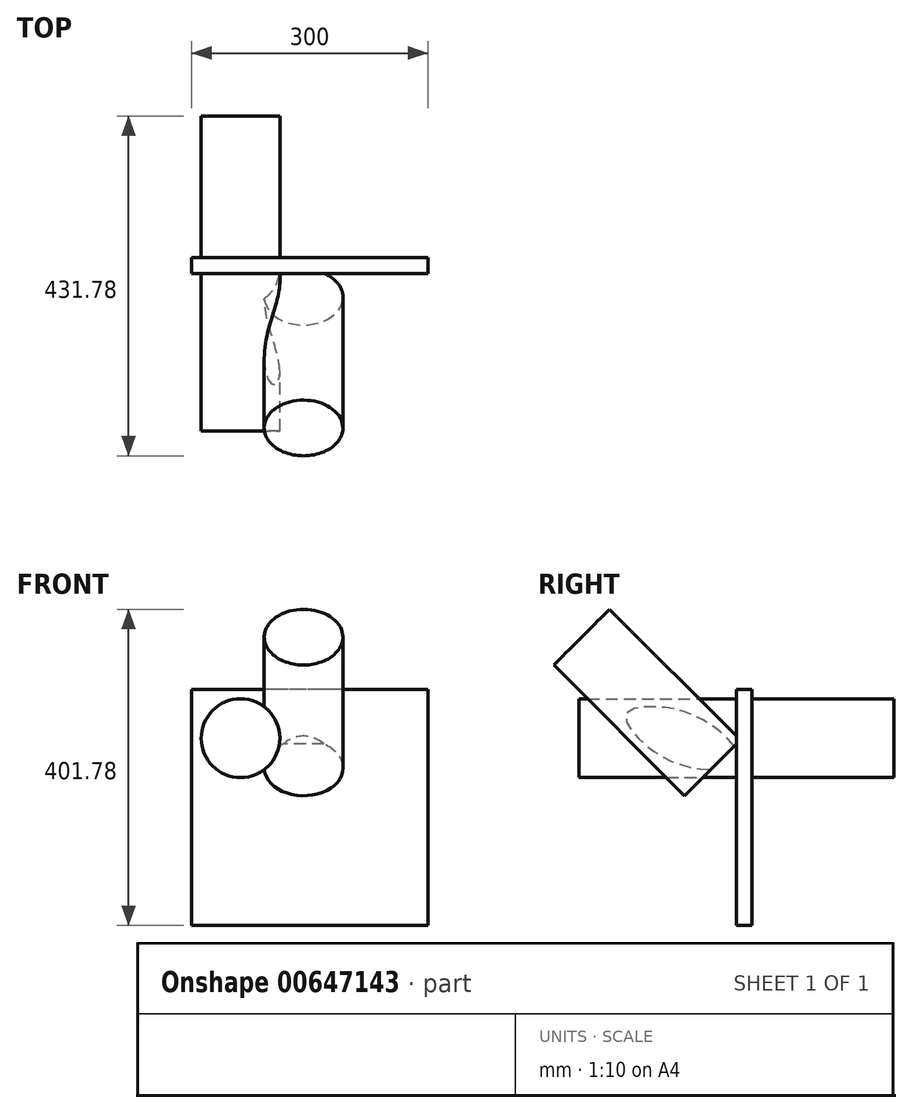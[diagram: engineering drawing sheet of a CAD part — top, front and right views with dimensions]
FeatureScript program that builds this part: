
annotation { "Feature Type Name" : "Feature", "Feature Type Description" : "" }
export const myFeature = defineFeature(function(context is Context, id is Id, definition is map)
    precondition{}
    {
        {
            var Q0;
            Q0=qCreatedBy(makeId("Front.planeOp"),FACE);
            var sketch = newSketch(context, id + "F0", { "sketchPlane" : qUnion([Q0])});
            skLineSegment(sketch, "E0.bottom", {"start": v(157.9, 150) * mm, "end": v(-142.1, 150) * mm});
            skLineSegment(sketch, "E0.top", {"start": v(157.9, -150) * mm, "end": v(-142.1, -150) * mm});
            skLineSegment(sketch, "E0.left", {"start": v(157.9, 150) * mm, "end": v(157.9, -150) * mm});
            skLineSegment(sketch, "E0.right", {"start": v(-142.1, 150) * mm, "end": v(-142.1, -150) * mm});
            skPoint(sketch, "E0.middle", {"position": v(7.9, 0) * mm});
            skSolve(sketch);
        }
        {
            var Q0;
            Q0=qSketchRegion(id+"F0",true);
            extrude(context, id + "F1", {"entities" : qUnion([Q0]), "depth" : 20 * mm, "offsetDistance" : 25 * mm});
        }
        {
            var Q0;
            Q0=makeQuery(id+"F1.opExtrude","CAP_FACE",FACE,{"disambiguationData":[OSD([sQuery(id+"F0.wireOp",EDGE,"E0.bottom"),sQuery(id+"F0.wireOp",EDGE,"E0.top"),sQuery(id+"F0.wireOp",EDGE,"E0.left"),sQuery(id+"F0.wireOp",EDGE,"E0.right")])],"isStart":false});
            var sketch = newSketch(context, id + "F2", { "sketchPlane" : qUnion([Q0])});
            skCircle(sketch, "E1", {"center": v(-80.1, 88) * mm, "radius": 50 * mm});
            skSolve(sketch);
        }
        {
            var Q0;
            Q0=makeQuery(id+"F2.imprint","IMPRINT",FACE,{"disambiguationData":[TD([[makeQuery(id+"F2.imprint","IMPRINT",EDGE,{"derivedFrom":sQuery(id+"F2.wireOp",EDGE,"E1")}),1.0]])]});
            extrude(context, id + "F3", {"entities" : qUnion([Q0]), "operationType" : NewBodyOperationType.ADD, "depth" : 200 * mm, "offsetDistance" : 25 * mm, "hasSecondDirection" : true, "secondDirectionOppositeDirection" : true, "secondDirectionDepth" : 200 * mm});
        }
        {
            var Q0;
            Q0=makeQuery(id+"F1.opExtrude","CAP_EDGE",EDGE,{"disambiguationData":[OSD([sQuery(id+"F0.wireOp",EDGE,"E0.bottom")])],"isStart":true});
            cPlane(context, id + "F4", {"entities" : qUnion([Q0]), "cplaneType" : CPlaneType.LINE_ANGLE, "offset" : 25 * mm, "angle" : 45 * degree, "width" : 150 * mm, "height" : 150 * mm});
        }
        {
            var Q0;
            Q0=qCreatedBy(id+"F4.planeOp",FACE);
            var sketch = newSketch(context, id + "F5", { "sketchPlane" : qUnion([Q0])});
            skCircle(sketch, "E2", {"center": v(0, 0) * mm, "radius": 50 * mm});
            skSolve(sketch);
        }
        {
            var Q0;
            Q0=qSketchRegion(id+"F5",true);
            extrude(context, id + "F6", {"entities" : qUnion([Q0]), "operationType" : NewBodyOperationType.ADD, "depth" : 200 * mm, "offsetDistance" : 25 * mm, "hasSecondDirection" : true, "secondDirectionOppositeDirection" : true, "secondDirectionDepth" : 35 * mm});
        }
    });
